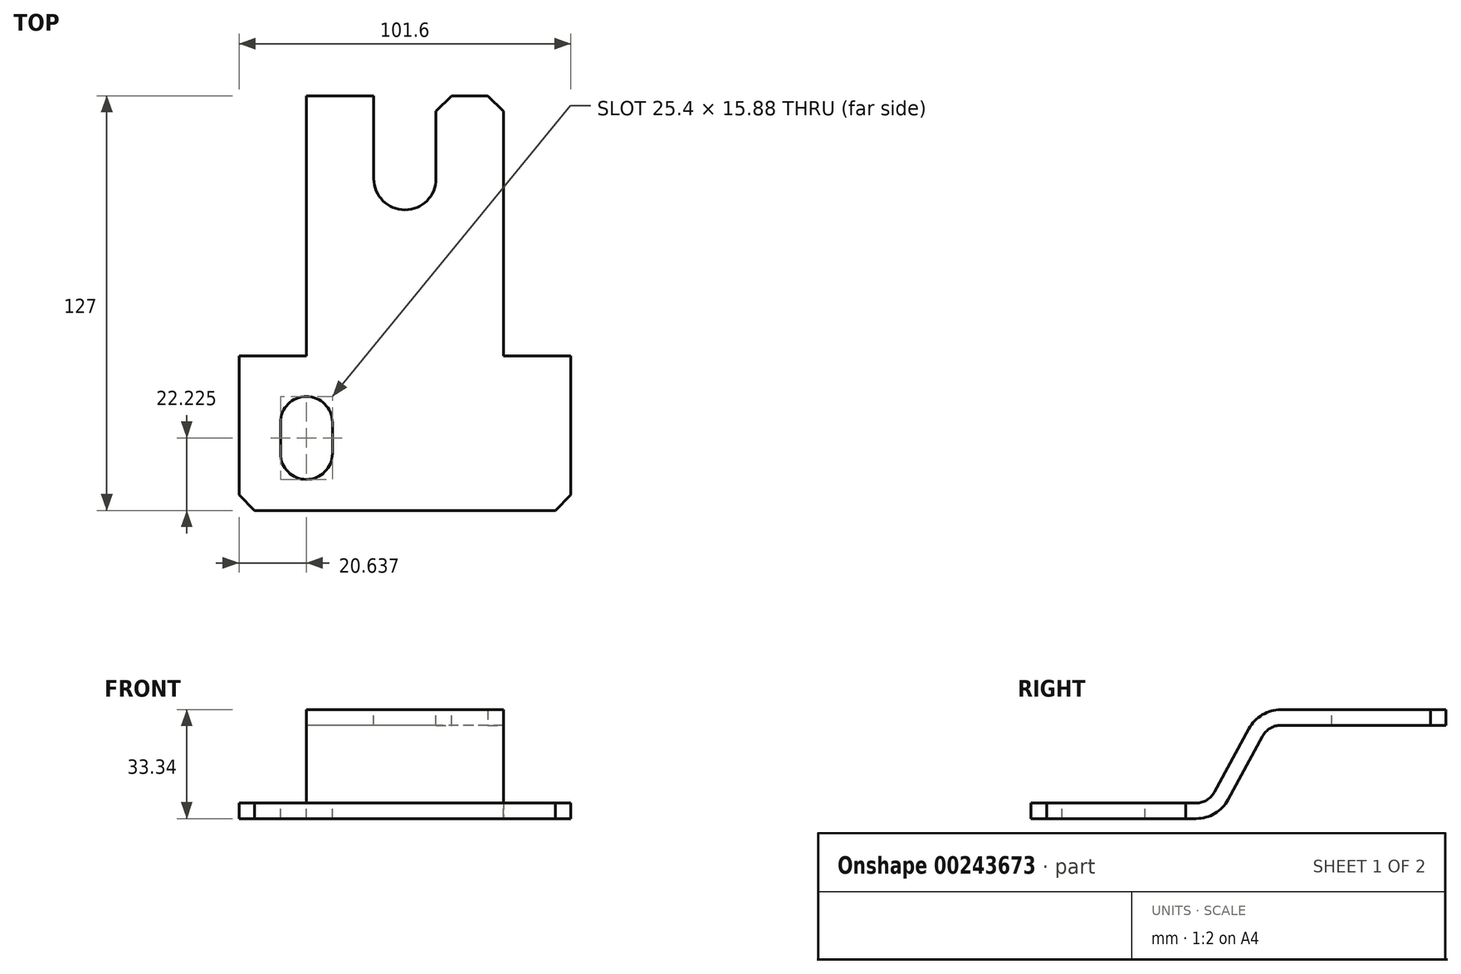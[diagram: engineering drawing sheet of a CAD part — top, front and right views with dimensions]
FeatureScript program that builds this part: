
annotation { "Feature Type Name" : "Feature", "Feature Type Description" : "" }
export const myFeature = defineFeature(function(context is Context, id is Id, definition is map)
    precondition{}
    {
        {
            var Q0;
            Q0=qCreatedBy(makeId("Right.planeOp"),FACE);
            var sketch = newSketch(context, id + "F0", { "sketchPlane" : qUnion([Q0])});
            skLineSegment(sketch, "E0", {"start": v(-63.5, 0) * mm, "end": v(63.5, 0) * mm, "construction": true});
            skLineSegment(sketch, "E1", {"start": v(-63.5, 0) * mm, "end": v(-63.5, 4.76) * mm});
            skLineSegment(sketch, "E2", {"start": v(-63.5, 4.76) * mm, "end": v(-12.96, 4.76) * mm});
            skLineSegment(sketch, "E3", {"start": v(-7.38, 8.08) * mm, "end": v(6.35, 33.34) * mm});
            skLineSegment(sketch, "E4", {"start": v(6.35, 33.34) * mm, "end": v(63.5, 33.34) * mm});
            skLineSegment(sketch, "E5", {"start": v(63.5, 33.34) * mm, "end": v(63.5, 28.58) * mm});
            skLineSegment(sketch, "E6", {"start": v(63.5, 28.58) * mm, "end": v(12.96, 28.58) * mm});
            skLineSegment(sketch, "E7", {"start": v(-63.5, 0) * mm, "end": v(-6.35, 0) * mm});
            skLineSegment(sketch, "E8", {"start": v(-6.35, 0) * mm, "end": v(7.38, 25.26) * mm});
            skPoint(sketch, "E9.visualSharp", {"position": v(-9.18, 4.76) * mm});
            skArc(sketch, "E9.filletArc", {"start": v(-12.96, 4.76) * mm, "mid": v(-9.71, 5.65) * mm, "end": v(-7.38, 8.08) * mm});
            skPoint(sketch, "E10.visualSharp", {"position": v(9.18, 28.58) * mm});
            skArc(sketch, "E10.filletArc", {"start": v(12.96, 28.58) * mm, "mid": v(9.71, 27.68) * mm, "end": v(7.38, 25.26) * mm});
            skSolve(sketch);
        }
        {
            var Q0;
            Q0=makeQuery(id+"F0.imprint","IMPRINT",FACE,{"disambiguationData":[TD([[makeQuery(id+"F0.imprint","IMPRINT",EDGE,{"derivedFrom":sQuery(id+"F0.wireOp",EDGE,"E1")}),-1.0]])]});
            extrude(context, id + "F1", {"entities" : qUnion([Q0]), "endBound" : BoundingType.SYMMETRIC, "depth" : 101.6 * mm});
        }
        {
            var Q0;
            Q0=makeQuery(id+"F1.opExtrude","SWEPT_EDGE",EDGE,{"disambiguationData":[OSD([sQuery(id+"F0.wireOp",EDGE,"E3"),sQuery(id+"F0.wireOp",EDGE,"E4")])]});
            var Q1;
            Q1=makeQuery(id+"F1.opExtrude","SWEPT_EDGE",EDGE,{"disambiguationData":[OSD([sQuery(id+"F0.wireOp",EDGE,"E7"),sQuery(id+"F0.wireOp",EDGE,"E8")])]});
            fillet(context, id + "F2", {"entities" : qUnion([Q0, Q1]), "radius" : 11.1 * mm, "tangentPropagation" : true, "allowEdgeOverflow" : false});
        }
        {
            var Q0;
            Q0=makeQuery(id+"F1.opExtrude","SWEPT_FACE",FACE,{"disambiguationData":[OSD([sQuery(id+"F0.wireOp",EDGE,"E4")])]});
            var sketch = newSketch(context, id + "F3", { "sketchPlane" : qUnion([Q0])});
            skLineSegment(sketch, "E11", {"start": v(-30.16, -16.13) * mm, "end": v(-30.16, 63.5) * mm});
            skLineSegment(sketch, "E12", {"start": v(-30.16, 63.5) * mm, "end": v(-50.8, 63.5) * mm});
            skLineSegment(sketch, "E13", {"start": v(-50.8, 63.5) * mm, "end": v(-50.8, -16.13) * mm});
            skLineSegment(sketch, "E14", {"start": v(-50.8, -16.13) * mm, "end": v(-30.16, -16.13) * mm});
            skLineSegment(sketch, "E15.bottom", {"start": v(50.8, 63.5) * mm, "end": v(30.16, 63.5) * mm});
            skLineSegment(sketch, "E15.top", {"start": v(50.8, -16.13) * mm, "end": v(30.16, -16.13) * mm});
            skLineSegment(sketch, "E15.left", {"start": v(50.8, 63.5) * mm, "end": v(50.8, -16.13) * mm});
            skLineSegment(sketch, "E15.right", {"start": v(30.16, 63.5) * mm, "end": v(30.16, -16.13) * mm});
            skLineSegment(sketch, "E16", {"start": v(30.16, 63.5) * mm, "end": v(-30.16, 63.5) * mm, "construction": true});
            skLineSegment(sketch, "E17", {"start": v(0, 0) * mm, "end": v(0, 63.5) * mm, "construction": true});
            skLineSegment(sketch, "E18", {"start": v(0, -63.5) * mm, "end": v(0, -41.27) * mm, "construction": true});
            skLineSegment(sketch, "E19", {"start": v(-30.16, -41.27) * mm, "end": v(30.16, -41.27) * mm, "construction": true});
            skPoint(sketch, "E20.middle", {"position": v(30.16, -41.27) * mm});
            skLineSegment(sketch, "E21.bottom", {"start": v(-38.1, -46.04) * mm, "end": v(-22.23, -46.04) * mm, "construction": true});
            skLineSegment(sketch, "E21.top", {"start": v(-38.1, -36.51) * mm, "end": v(-22.23, -36.51) * mm, "construction": true});
            skLineSegment(sketch, "E21.left", {"start": v(-38.1, -46.04) * mm, "end": v(-38.1, -36.51) * mm});
            skLineSegment(sketch, "E21.right", {"start": v(-22.23, -46.04) * mm, "end": v(-22.23, -36.51) * mm});
            skPoint(sketch, "E21.middle", {"position": v(-30.16, -41.27) * mm});
            skArc(sketch, "E22", {"start": v(-38.1, -46.04) * mm, "mid": v(-30.16, -53.97) * mm, "end": v(-22.23, -46.04) * mm});
            skArc(sketch, "E23", {"start": v(-22.23, -36.51) * mm, "mid": v(-30.16, -28.57) * mm, "end": v(-38.1, -36.51) * mm});
            skArc(sketch, "E24.MirrorCS", {"start": v(22.23, -36.51) * mm, "mid": v(30.16, -28.57) * mm, "end": v(38.1, -36.51) * mm});
            skLineSegment(sketch, "E25.MirrorCS", {"start": v(38.1, -36.51) * mm, "end": v(22.23, -36.51) * mm, "construction": true});
            skLineSegment(sketch, "E26.MirrorCS", {"start": v(38.1, -46.04) * mm, "end": v(38.1, -36.51) * mm});
            skLineSegment(sketch, "E27.MirrorCS", {"start": v(22.23, -46.04) * mm, "end": v(22.23, -36.51) * mm});
            skArc(sketch, "E28.MirrorCS", {"start": v(38.1, -46.04) * mm, "mid": v(30.16, -53.97) * mm, "end": v(22.23, -46.04) * mm});
            skLineSegment(sketch, "E29.MirrorCS", {"start": v(38.1, -46.04) * mm, "end": v(22.23, -46.04) * mm, "construction": true});
            skCircle(sketch, "E30", {"center": v(0, 38.1) * mm, "radius": 9.53 * mm});
            skLineSegment(sketch, "E31", {"start": v(-9.53, 63.5) * mm, "end": v(-9.53, 38.1) * mm});
            skLineSegment(sketch, "E32", {"start": v(9.53, 38.1) * mm, "end": v(9.53, 63.5) * mm});
            skSolve(sketch);
        }
        {
            var Q0;
            Q0=makeQuery(id+"F3.imprint","IMPRINT",FACE,{"disambiguationData":[TD([[makeQuery(id+"F3.imprint","IMPRINT",EDGE,{"derivedFrom":sQuery(id+"F3.wireOp",EDGE,"E21.left")}),-1.0]])]});
            var Q1;
            Q1=makeQuery(id+"F3.imprint","IMPRINT",FACE,{"disambiguationData":[TD([[makeQuery(id+"F3.imprint","IMPRINT",EDGE,{"derivedFrom":sQuery(id+"F3.wireOp",EDGE,"E24.MirrorCS")}),-1.0]])]});
            var Q2;
            {var subQ0=sQuery(id+"F3.wireOp",EDGE,"E14");Q2=makeQuery(id+"F3.imprint","IMPRINT",FACE,{"disambiguationData":[TD([[makeQuery(id+"F3.imprint","IMPRINT",EDGE,{"derivedFrom":subQ0}),1.0]])]});}
            var Q3;
            {var subQ0=sQuery(id+"F3.wireOp",EDGE,"E15.top");Q3=makeQuery(id+"F3.imprint","IMPRINT",FACE,{"disambiguationData":[TD([[makeQuery(id+"F3.imprint","IMPRINT",EDGE,{"derivedFrom":subQ0}),-1.0]])]});}
            var Q4;
            {var subQ0=sQuery(id+"F3.wireOp",EDGE,"E30");var subQ1=makeQuery(id+"F3.imprint","INTERSECT",VERTEX,{"derivedFrom":[subQ0,sQuery(id+"F3.wireOp",EDGE,"E31")]});Q4=makeQuery(id+"F3.imprint","IMPRINT",FACE,{"disambiguationData":[TD([[makeQuery(id+"F3.imprint","IMPRINT",EDGE,{"disambiguationData":[TD([[subQ1,1.0]])],"derivedFrom":subQ0}),1.0]])]});}
            var Q5;
            {var subQ0=sQuery(id+"F3.wireOp",EDGE,"E31");Q5=makeQuery(id+"F3.imprint","IMPRINT",FACE,{"disambiguationData":[TD([[makeQuery(id+"F3.imprint","IMPRINT",EDGE,{"derivedFrom":subQ0}),1.0]])]});}
            var Q6;
            {var subQ0=sQuery(id+"F3.wireOp",EDGE,"E12");Q6=makeQuery(id+"F3.imprint","IMPRINT",FACE,{"disambiguationData":[TD([[makeQuery(id+"F3.imprint","IMPRINT",EDGE,{"derivedFrom":subQ0}),1.0]])]});}
            var Q7;
            {var subQ0=sQuery(id+"F3.wireOp",EDGE,"E15.bottom");Q7=makeQuery(id+"F3.imprint","IMPRINT",FACE,{"disambiguationData":[TD([[makeQuery(id+"F3.imprint","IMPRINT",EDGE,{"derivedFrom":subQ0}),1.0]])]});}
            extrude(context, id + "F4", {"entities" : qUnion([Q0, Q1, Q2, Q3, Q4, Q5, Q6, Q7]), "operationType" : NewBodyOperationType.REMOVE, "endBound" : BoundingType.THROUGH_ALL, "oppositeDirection" : true, "depth" : 25.4 * mm});
        }
        {
            var Q0;
            Q0=makeQuery(id+"F1.opExtrude","CAP_EDGE",EDGE,{"disambiguationData":[OSD([sQuery(id+"F0.wireOp",EDGE,"E1")])],"isStart":false});
            var Q1;
            Q1=makeQuery(id+"F4.boolean.opBoolean","COPY",EDGE,{"derivedFrom":makeQuery(id+"F4.opExtrude","SWEPT_EDGE",EDGE,{"disambiguationData":[OSD([sQuery(id+"F3.wireOp",EDGE,"E15.top"),sQuery(id+"F3.wireOp",EDGE,"E15.left")])]})});
            var Q2;
            Q2=makeQuery(id+"F1.opExtrude","CAP_EDGE",EDGE,{"disambiguationData":[OSD([sQuery(id+"F0.wireOp",EDGE,"E1")])],"isStart":true});
            var Q3;
            Q3=makeQuery(id+"F4.boolean.opBoolean","COPY",EDGE,{"derivedFrom":makeQuery(id+"F4.opExtrude","SWEPT_EDGE",EDGE,{"disambiguationData":[OSD([sQuery(id+"F3.wireOp",EDGE,"E13"),sQuery(id+"F3.wireOp",EDGE,"E14")])]})});
            var Q4;
            Q4=makeQuery(id+"F4.boolean.opBoolean","COPY",EDGE,{"derivedFrom":makeQuery(id+"F4.opExtrude","SWEPT_EDGE",EDGE,{"disambiguationData":[OSD([sQuery(id+"F0.wireOp",EDGE,"E4"),sQuery(id+"F0.wireOp",EDGE,"E5"),sQuery(id+"F3.wireOp",EDGE,"E15.bottom"),sQuery(id+"F3.wireOp",EDGE,"E15.right")])]})});
            var Q5;
            Q5=makeQuery(id+"F4.boolean.opBoolean","COPY",EDGE,{"derivedFrom":makeQuery(id+"F4.opExtrude","SWEPT_EDGE",EDGE,{"disambiguationData":[OSD([sQuery(id+"F0.wireOp",EDGE,"E4"),sQuery(id+"F0.wireOp",EDGE,"E5"),sQuery(id+"F3.wireOp",EDGE,"E32")])]})});
            var Q6;
            Q6=makeQuery(id+"F4.boolean.opBoolean","COPY",EDGE,{"derivedFrom":makeQuery(id+"F4.opExtrude","SWEPT_EDGE",EDGE,{"disambiguationData":[OSD([sQuery(id+"F0.wireOp",EDGE,"E4"),sQuery(id+"F0.wireOp",EDGE,"E5"),sQuery(id+"F3.wireOp",EDGE,"E31")])]})});
            var Q7;
            Q7=makeQuery(id+"F4.boolean.opBoolean","COPY",EDGE,{"derivedFrom":makeQuery(id+"F4.opExtrude","SWEPT_EDGE",EDGE,{"disambiguationData":[OSD([sQuery(id+"F0.wireOp",EDGE,"E4"),sQuery(id+"F0.wireOp",EDGE,"E5"),sQuery(id+"F3.wireOp",EDGE,"E11"),sQuery(id+"F3.wireOp",EDGE,"E12")])]})});
            chamfer(context, id + "F5", {"entities" : qUnion([Q0, Q1, Q2, Q3, Q4, Q5, Q6, Q7]), "width" : 4.76 * mm, "tangentPropagation" : true});
        }
    });
